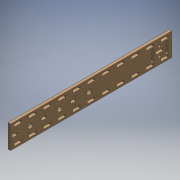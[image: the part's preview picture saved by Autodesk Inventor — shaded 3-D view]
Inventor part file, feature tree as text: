
AUTODESK INVENTOR PART (.ipt)
format: ipt  version: 2016 (Build 200138000, 138)  size: 402,944 bytes
history: native  units: mm
features: extrude x1, sketch x1
ambient origin geometry x8: Origin, YZ Plane, XZ Plane, XY Plane, X Axis, Y Axis, Z Axis, Center Point
bodies: Body1 (feature_tree)
feature tree (2):
  extrude  "Extrusion8"  Depth=13.147317mm
  sketch  "Sketch1"  dims[d1=12.0mm d2=13.147317mm d3=6.3261mm d4=4.0mm d5=22.098mm d6=34.539mm d8=37.0mm d9=7.0mm d12=18.958829mm d13=6.3261mm d14=9.479415mm d15=20.0mm d17=37.917659mm d18=20.0mm d20=43.39mm d23=3.0mm d24=15.5mm d26=60.0mm d28=360.0deg d32=2.5mm d33=1.1mm d34=2.0mm d35=10.0mm d77=24.149mm d78=29.89mm d80=6.39mm d81=9.479415mm d83=18.958829mm d84=6.39mm d87=30.0mm d89=75.835317mm d90=10.0mm d92=10.0mm d94=151.670635mm d97=63.266488mm d98=227.505952mm d101=60.0mm d103=37.917659mm d104=10.0mm d106=10.0mm d112=24.0mm d113=0.0mm d116=18.39mm d170=6.6675mm d172=6.39mm d173=0.0mm d176=34.539mm]
